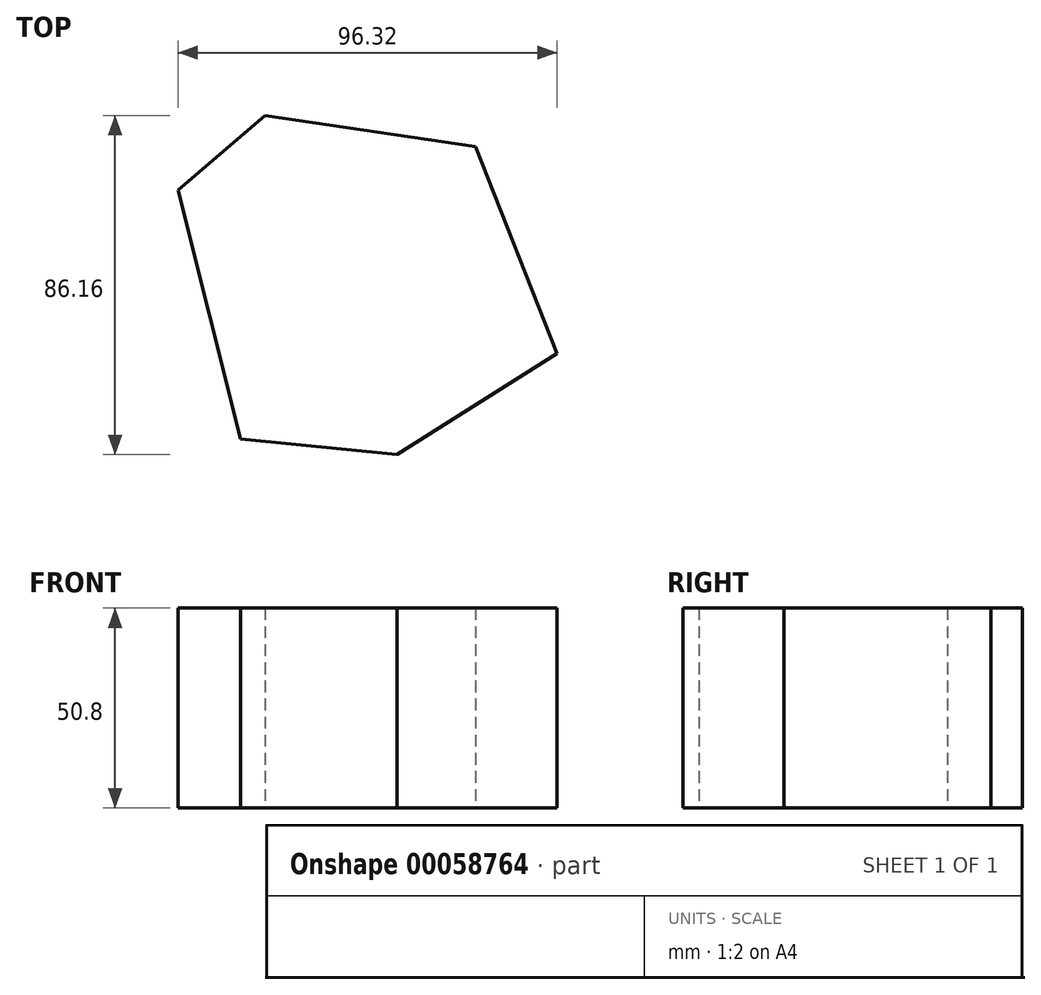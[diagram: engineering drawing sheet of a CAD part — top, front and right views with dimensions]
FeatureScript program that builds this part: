
annotation { "Feature Type Name" : "Feature", "Feature Type Description" : "" }
export const myFeature = defineFeature(function(context is Context, id is Id, definition is map)
    precondition{}
    {
        {
            var Q0;
            Q0=qCreatedBy(makeId("Top.planeOp"),FACE);
            var sketch = newSketch(context, id + "F0", { "sketchPlane" : qUnion([Q0])});
            skLineSegment(sketch, "E0", {"start": v(-46.4, 26.73) * mm, "end": v(-24.3, 45.73) * mm});
            skLineSegment(sketch, "E1", {"start": v(-24.3, 45.73) * mm, "end": v(29.16, 37.78) * mm});
            skLineSegment(sketch, "E2", {"start": v(29.16, 37.78) * mm, "end": v(49.93, -14.8) * mm});
            skLineSegment(sketch, "E3", {"start": v(49.93, -14.8) * mm, "end": v(9.28, -40.43) * mm});
            skLineSegment(sketch, "E4", {"start": v(9.28, -40.43) * mm, "end": v(-30.49, -36.45) * mm});
            skLineSegment(sketch, "E5", {"start": v(-30.49, -36.45) * mm, "end": v(-46.4, 26.73) * mm});
            skSolve(sketch);
        }
        {
            var Q0;
            Q0 = qSketchRegion(id + "F0", true);
            extrude(context, id + "F1", {"entities" : qUnion([Q0]), "depth" : 50.8 * mm});
        }
    });
